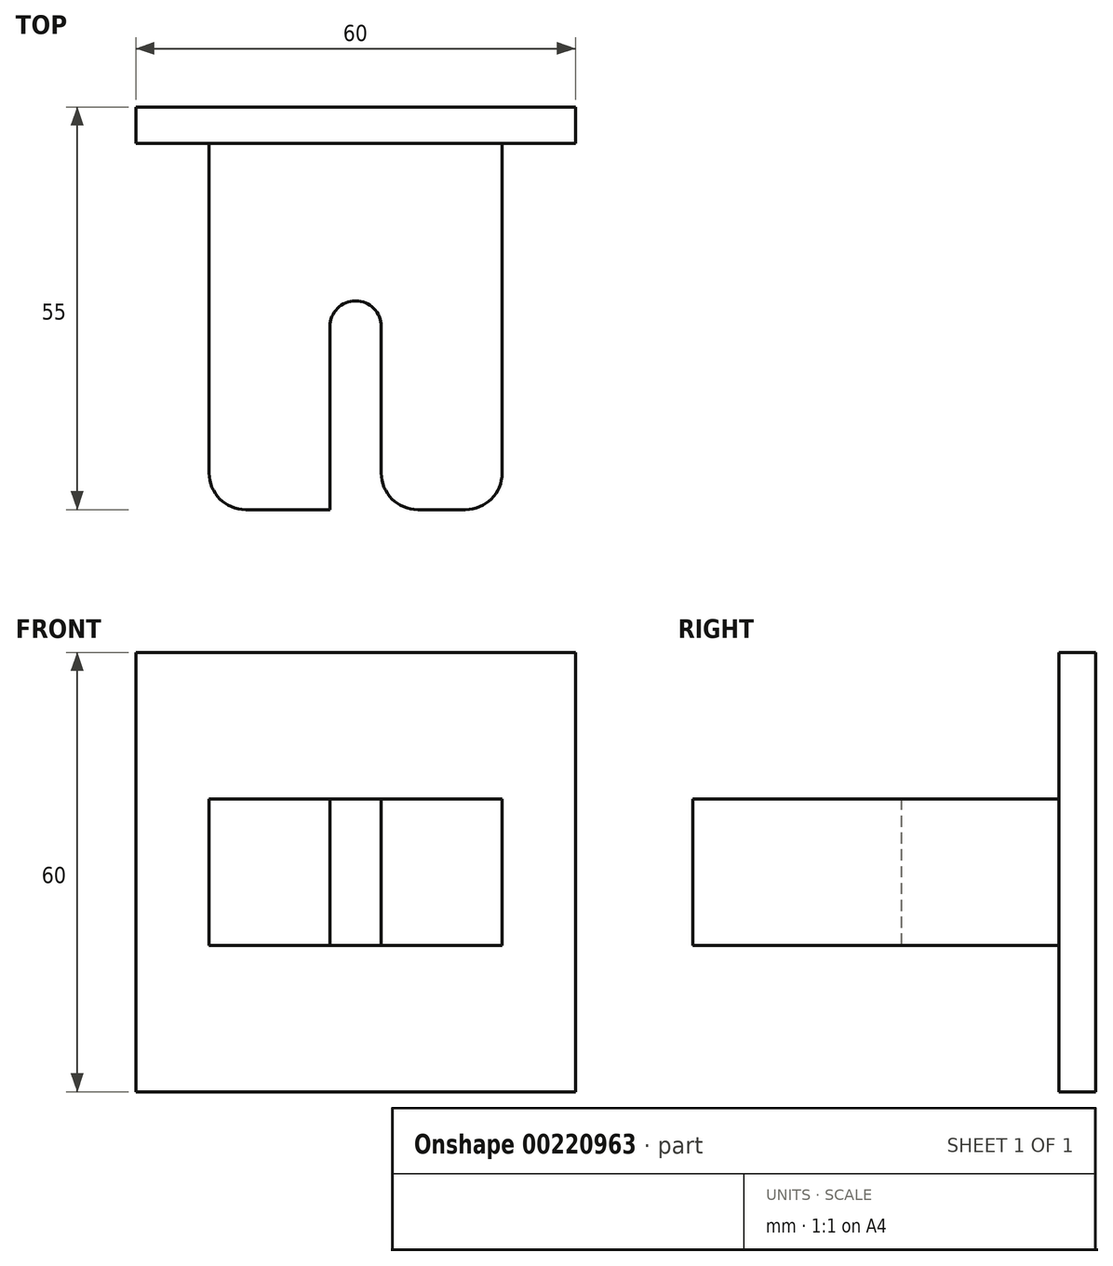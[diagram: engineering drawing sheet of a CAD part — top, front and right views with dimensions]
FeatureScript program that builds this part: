
annotation { "Feature Type Name" : "Feature", "Feature Type Description" : "" }
export const myFeature = defineFeature(function(context is Context, id is Id, definition is map)
    precondition{}
    {
        {
            var Q0;
            Q0=qCreatedBy(makeId("Front.planeOp"),FACE);
            var sketch = newSketch(context, id + "F0", { "sketchPlane" : qUnion([Q0])});
            skLineSegment(sketch, "E0", {"start": v(0, 0) * mm, "end": v(0, 10) * mm});
            skLineSegment(sketch, "E1", {"start": v(0, 10) * mm, "end": v(20, 10) * mm});
            skLineSegment(sketch, "E2", {"start": v(20, 10) * mm, "end": v(20, -10) * mm});
            skLineSegment(sketch, "E3", {"start": v(20, -10) * mm, "end": v(-20, -10) * mm});
            skLineSegment(sketch, "E4", {"start": v(-20, -10) * mm, "end": v(-20, 10) * mm});
            skLineSegment(sketch, "E5", {"start": v(-20, 10) * mm, "end": v(0, 10) * mm});
            skSolve(sketch);
        }
        {
            var Q0;
            Q0=makeQuery(id+"F0.imprint","IMPRINT",FACE,{"disambiguationData":[TD([[makeQuery(id+"F0.imprint","IMPRINT",EDGE,{"derivedFrom":sQuery(id+"F0.wireOp",EDGE,"E1")}),-1.0]])]});
            extrude(context, id + "F1", {"entities" : qUnion([Q0]), "depth" : 50 * mm, "offsetDistance" : 25 * mm});
        }
        {
            var Q0;
            Q0=makeQuery(id+"F1.opExtrude","SWEPT_FACE",FACE,{"disambiguationData":[OSD([sQuery(id+"F0.wireOp",EDGE,"E3")])]});
            var sketch = newSketch(context, id + "F2", { "sketchPlane" : qUnion([Q0])});
            skLineSegment(sketch, "E6", {"start": v(-3.5, 25) * mm, "end": v(-3.5, 50) * mm});
            skLineSegment(sketch, "E7", {"start": v(3.5, 25) * mm, "end": v(3.5, 50) * mm});
            skArc(sketch, "E8", {"start": v(-3.5, 25) * mm, "mid": v(0, 21.5) * mm, "end": v(3.5, 25) * mm});
            skLineSegment(sketch, "E9", {"start": v(-3.5, 50) * mm, "end": v(3.5, 50) * mm});
            skSolve(sketch);
        }
        {
            var Q0;
            Q0 = qSketchRegion(id + "F2", true);
            extrude(context, id + "F3", {"entities" : qUnion([Q0]), "operationType" : NewBodyOperationType.REMOVE, "oppositeDirection" : true, "depth" : 25 * mm, "offsetDistance" : 25 * mm});
        }
        {
            var Q0;
            Q0=makeQuery(id+"F1.opExtrude","CAP_FACE",FACE,{"disambiguationData":[OSD([sQuery(id+"F0.wireOp",EDGE,"E1"),sQuery(id+"F0.wireOp",EDGE,"E2"),sQuery(id+"F0.wireOp",EDGE,"E3"),sQuery(id+"F0.wireOp",EDGE,"E4"),sQuery(id+"F0.wireOp",EDGE,"E5")])],"isStart":true});
            var sketch = newSketch(context, id + "F4", { "sketchPlane" : qUnion([Q0])});
            skLineSegment(sketch, "E10", {"start": v(0, 0) * mm, "end": v(-30, 0) * mm});
            skPoint(sketch, "E10.endSnap0", {"position": v(-20, 0) * mm});
            skLineSegment(sketch, "E11", {"start": v(-30, 0) * mm, "end": v(-30, 30) * mm});
            skLineSegment(sketch, "E12.bottom", {"start": v(-30, 30) * mm, "end": v(30, 30) * mm});
            skLineSegment(sketch, "E12.top", {"start": v(-30, -30) * mm, "end": v(30, -30) * mm});
            skLineSegment(sketch, "E12.left", {"start": v(-30, 30) * mm, "end": v(-30, -30) * mm});
            skLineSegment(sketch, "E12.right", {"start": v(30, 30) * mm, "end": v(30, -30) * mm});
            skSolve(sketch);
        }
        {
            var Q0;
            {var subQ5=makeQuery(id+"F1.opExtrude","CAP_EDGE",EDGE,{"disambiguationData":[OSD([sQuery(id+"F0.wireOp",EDGE,"E3")])],"isStart":true});var subQ6=makeQuery(id+"F4.imprint","IMPRINT",EDGE,{"derivedFrom":subQ5});Q0=qUnion([makeQuery(id+"F4.imprint","IMPRINT",FACE,{"disambiguationData":[TD([[makeQuery(id+"F4.imprint","IMPRINT",EDGE,{"derivedFrom":sQuery(id+"F4.wireOp",EDGE,"E11")}),-1.0]])]}),makeQuery(id+"F4.imprint","IMPRINT",FACE,{"disambiguationData":[TD([[subQ6,1.0]])]})]);}
            extrude(context, id + "F5", {"entities" : qUnion([Q0]), "operationType" : NewBodyOperationType.ADD, "depth" : 5 * mm, "offsetDistance" : 25 * mm});
        }
        {
            var Q0;
            Q0=makeQuery(id+"F1.opExtrude","CAP_EDGE",EDGE,{"disambiguationData":[OSD([sQuery(id+"F0.wireOp",EDGE,"E2")])],"isStart":false});
            var Q1;
            Q1=makeQuery(id+"F3.boolean.opBoolean","COPY",EDGE,{"derivedFrom":makeQuery(id+"F3.opExtrude","SWEPT_EDGE",EDGE,{"disambiguationData":[OSD([sQuery(id+"F0.wireOp",EDGE,"E3"),sQuery(id+"F2.wireOp",EDGE,"E7"),sQuery(id+"F2.wireOp",EDGE,"E9")])]})});
            var Q2;
            Q2=makeQuery(id+"F3.boolean.opBoolean","COPY",EDGE,{"derivedFrom":makeQuery(id+"F3.opExtrude","SWEPT_EDGE",EDGE,{"disambiguationData":[OSD([sQuery(id+"F0.wireOp",EDGE,"E3"),sQuery(id+"F2.wireOp",EDGE,"E6"),sQuery(id+"F2.wireOp",EDGE,"E9")])]})});
            var Q3;
            Q3=makeQuery(id+"F1.opExtrude","CAP_EDGE",EDGE,{"disambiguationData":[OSD([sQuery(id+"F0.wireOp",EDGE,"E4")])],"isStart":false});
            fillet(context, id + "F6", {"entities" : qUnion([Q0, Q1, Q2, Q3]), "radius" : 5 * mm, "tangentPropagation" : true, "allowEdgeOverflow" : false});
        }
    });
